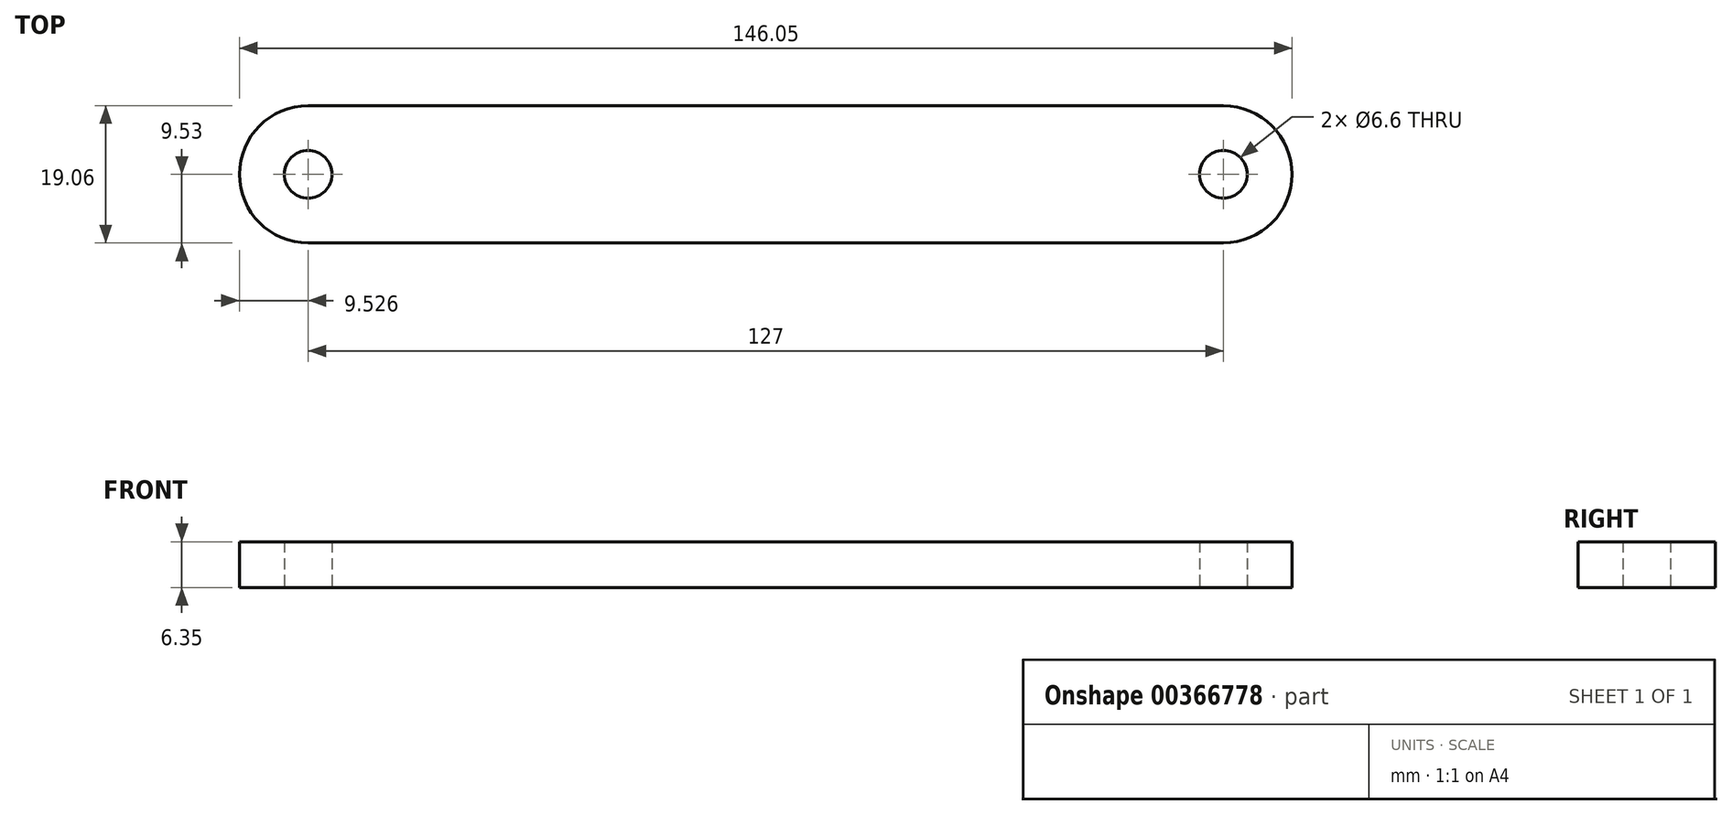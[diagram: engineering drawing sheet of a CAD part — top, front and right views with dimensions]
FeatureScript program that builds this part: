
annotation { "Feature Type Name" : "Feature", "Feature Type Description" : "" }
export const myFeature = defineFeature(function(context is Context, id is Id, definition is map)
    precondition{}
    {
        {
            var Q0;
            Q0=qCreatedBy(makeId("Top.planeOp"),FACE);
            var sketch = newSketch(context, id + "F0", { "sketchPlane" : qUnion([Q0])});
            skCircle(sketch, "E0", {"center": v(-78.14, 0) * mm, "radius": 3.3 * mm});
            skCircle(sketch, "E1", {"center": v(48.86, 0) * mm, "radius": 3.3 * mm});
            skCircle(sketch, "E2", {"center": v(-78.14, 0) * mm, "radius": 9.53 * mm});
            skCircle(sketch, "E3", {"center": v(48.86, 0) * mm, "radius": 9.53 * mm});
            skLineSegment(sketch, "E4", {"start": v(-78.14, 9.52) * mm, "end": v(48.86, 9.53) * mm});
            skLineSegment(sketch, "E5", {"start": v(-78.14, -9.53) * mm, "end": v(48.86, -9.52) * mm});
            skLineSegment(sketch, "E6", {"start": v(-14.64, 9.52) * mm, "end": v(-14.64, -9.52) * mm, "construction": true});
            skSolve(sketch);
        }
        {
            var Q0;
            Q0=makeQuery(id+"F0.imprint","IMPRINT",FACE,{"disambiguationData":[TD([[makeQuery(id+"F0.imprint","IMPRINT",EDGE,{"derivedFrom":sQuery(id+"F0.wireOp",EDGE,"E0")}),-1.0]])]});
            var Q1;
            Q1=makeQuery(id+"F0.imprint","IMPRINT",FACE,{"disambiguationData":[TD([[makeQuery(id+"F0.imprint","IMPRINT",EDGE,{"derivedFrom":sQuery(id+"F0.wireOp",EDGE,"E1")}),-1.0]])]});
            var Q2;
            {var subQ0=sQuery(id+"F0.wireOp",EDGE,"E4");Q2=makeQuery(id+"F0.imprint","IMPRINT",FACE,{"disambiguationData":[TD([[makeQuery(id+"F0.imprint","IMPRINT",EDGE,{"derivedFrom":subQ0}),-1.0]])]});}
            extrude(context, id + "F1", {"entities" : qUnion([Q0, Q1, Q2]), "depth" : 6.35 * mm});
        }
    });
